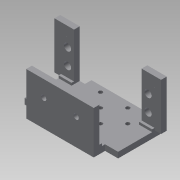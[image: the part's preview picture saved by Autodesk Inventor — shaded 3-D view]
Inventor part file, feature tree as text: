
AUTODESK INVENTOR PART (.ipt)
format: ipt  version: 2015 SP1 (Build 190203100, 203)  size: 387,584 bytes
history: native  units: in
note: dims shown in document units (in); Inventor stores cm internally (conversion verified against a paired STEP export)
features: sketch x16, extrude x15, mirror x7, projected_geometry x4, fillet x2, other x1, imported_body x1, reference x1
ambient origin geometry x8: Origin, YZ Plane, XZ Plane, XY Plane, X Axis, Y Axis, Z Axis, Center Point
bodies: Body1 (feature_tree)
feature tree (47):
  fillet  "Fillet5"  Radius=0.782in
  other  "asb-041"
  sketch  "Sketch1"  dims[d1=2.25in d2=0.0779in d3=0.0in]
  extrude  "Extrusion1"  Depth=2.25in TaperAngle=0.0deg
  sketch  "Sketch8"  dims[d17=1.624in d18=0.0in d19=0.0779in d20=0.0in]
  extrude  "Extrusion4"  Depth=0.0778in
  sketch  "Sketch10"  dims[d22=0.313in d23=0.0in d27=0.313in d28=0.0in]
  extrude  "Extrusion5"  Depth=1.624in TaperAngle=0.0deg
  extrude  "Extrusion6"  Depth=0.313in TaperAngle=0.0deg
  sketch  "Sketch14"  dims[d35=0.1378in d36=0.0in d37=0.1565in]
  extrude  "Extrusion7"  Depth=0.01in
  mirror  "Mirror2"
  sketch  "Sketch17"  dims[d38=0.1378in d39=0.0in d41=0.0591in d42=0.0591in]
  extrude  "Extrusion8"  Depth=0.1565in
  extrude  "Extrusion9"  Depth=0.0591in
  mirror  "Mirror3"
  fillet  "Fillet1"  Radius=0.0591in
  mirror  "Mirror4"
  extrude  "Extrusion10"  Depth=0.0591in
  extrude  "Extrusion11"  Depth=0.313in TaperAngle=0.0deg
  mirror  "Mirror5"
  sketch  "Sketch26"  dims[d55=0.313in d56=0.0in d57=0.1378in d58=0.0in]
  extrude  "Extrusion12"  Depth=1.624in TaperAngle=0.0deg
  sketch  "Sketch28"
  extrude  "Extrusion13"  Depth=0.1378in TaperAngle=0.0deg
  mirror  "Mirror6"
  extrude  "Extrusion14"  [1 undecoded]
  extrude  "Extrusion15"  [1 undecoded]
  extrude  "Extrusion16"  [1 undecoded]
  mirror  "Mirror7"
  extrude  "Extrusion17"  [1 undecoded]
  mirror  "Mirror8"
  imported_body  "Base1"
  sketch  "Sketch2"  dims[d14=0.0779in d15=0.0in d16=0.0778in]
  projected_geometry  "Projected Loop1"
  projected_geometry  "Projected Loop6"
  sketch  "Sketch13"  dims[d29=0.313in d30=0.0in d32=0.01in]
  projected_geometry  "Projected Loop7"
  projected_geometry  "Projected Loop8"
  sketch  "Sketch19"  dims[d43=1.624in d44=0.0in d46=0.0591in]
  sketch  "Sketch23"  dims[d47=0.0591in d48=0.313in d49=0.0in]
  reference  "Reference1"
  sketch  "Sketch24"  dims[d51=0.1378in d52=0.0in d53=1.624in d54=0.0in]
  sketch  "Sketch30"
  sketch  "Sketch31"
  sketch  "Sketch32"
  sketch  "Sketch33"
note: 4 required parameter values undecoded (feature->parameter linkage not recoverable at this tier; creation-order binding heuristic only, values carry confidence <= 0.55)
